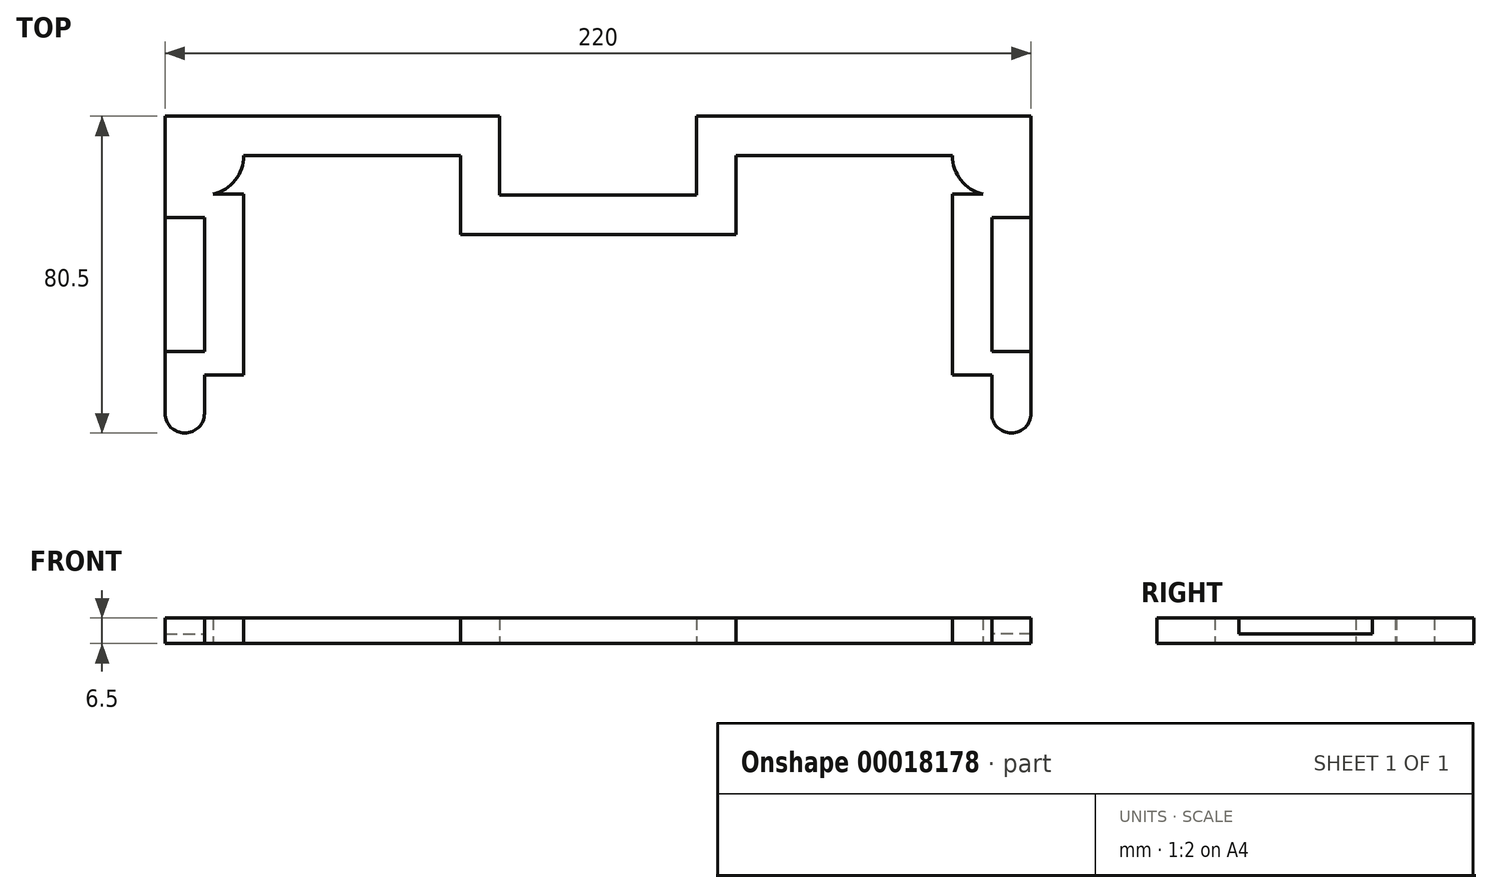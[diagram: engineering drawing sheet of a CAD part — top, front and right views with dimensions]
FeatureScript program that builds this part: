
annotation { "Feature Type Name" : "Feature", "Feature Type Description" : "" }
export const myFeature = defineFeature(function(context is Context, id is Id, definition is map)
    precondition{}
    {
        {
            var Q0;
            Q0=qCreatedBy(makeId("Top.planeOp"),FACE);
            var sketch = newSketch(context, id + "F0", { "sketchPlane" : qUnion([Q0])});
            skLineSegment(sketch, "E0.rect.top", {"start": v(110, 112.75) * mm, "end": v(25, 112.75) * mm});
            skLineSegment(sketch, "E0.rect.left", {"start": v(110, -112.75) * mm, "end": v(110, -112.72) * mm});
            skPoint(sketch, "E0.rect.middle", {"position": v(0, 0) * mm});
            skLineSegment(sketch, "E1.rect.top", {"start": v(-90, 102.75) * mm, "end": v(-35, 102.75) * mm});
            skLineSegment(sketch, "E1.rect.right", {"start": v(100, -102.75) * mm, "end": v(100, -102.7) * mm});
            skArc(sketch, "E2", {"start": v(90, 102.75) * mm, "mid": v(92.18, 96.51) * mm, "end": v(97.78, 93) * mm});
            skArc(sketch, "E3", {"start": v(-97.78, 93) * mm, "mid": v(-92.18, 96.51) * mm, "end": v(-90, 102.75) * mm});
            skLineSegment(sketch, "E4", {"start": v(0, -112.75) * mm, "end": v(0, 112.75) * mm, "construction": true});
            skLineSegment(sketch, "E5", {"start": v(-25, 112.75) * mm, "end": v(-25, 92.75) * mm});
            skLineSegment(sketch, "E6", {"start": v(-25, 92.75) * mm, "end": v(0, 92.75) * mm});
            skLineSegment(sketch, "E7", {"start": v(-35, 102.75) * mm, "end": v(-35, 82.75) * mm});
            skLineSegment(sketch, "E8", {"start": v(-35, 82.75) * mm, "end": v(0, 82.75) * mm});
            skLineSegment(sketch, "E9", {"start": v(-25, 92.75) * mm, "end": v(-25, 82.75) * mm, "construction": true});
            skLineSegment(sketch, "E10", {"start": v(-25, 92.75) * mm, "end": v(-35, 92.75) * mm, "construction": true});
            skLineSegment(sketch, "E11.MirrorCS", {"start": v(35, 82.75) * mm, "end": v(0, 82.75) * mm});
            skLineSegment(sketch, "E12.MirrorCS", {"start": v(25, 92.75) * mm, "end": v(0, 92.75) * mm});
            skLineSegment(sketch, "E13.MirrorCS", {"start": v(25, 112.75) * mm, "end": v(25, 92.75) * mm});
            skLineSegment(sketch, "E14.MirrorCS", {"start": v(35, 102.75) * mm, "end": v(35, 82.75) * mm});
            skLineSegment(sketch, "E15.trimOffspring", {"start": v(35, 102.75) * mm, "end": v(90, 102.75) * mm});
            skLineSegment(sketch, "E16.trimOffspring", {"start": v(-25, 112.75) * mm, "end": v(-110, 112.75) * mm});
            skLineSegment(sketch, "E17", {"start": v(126.96, -112.75) * mm, "end": v(126.96, 37.25) * mm, "construction": true});
            skLineSegment(sketch, "E18", {"start": v(126.96, 37.25) * mm, "end": v(110, 37.25) * mm, "construction": true});
            skLineSegment(sketch, "E19", {"start": v(110, 37.25) * mm, "end": v(100, 37.25) * mm, "construction": true});
            skArc(sketch, "E20", {"start": v(100, 37.25) * mm, "mid": v(105, 32.25) * mm, "end": v(110, 37.25) * mm});
            skArc(sketch, "E21.MirrorCS", {"start": v(-100, 37.25) * mm, "mid": v(-105, 32.25) * mm, "end": v(-110, 37.25) * mm});
            skLineSegment(sketch, "E22.trimOffspring", {"start": v(-100, 37.25) * mm, "end": v(-100, 47) * mm});
            skLineSegment(sketch, "E23.trimOffspring", {"start": v(-110, 37.25) * mm, "end": v(-110, 112.75) * mm});
            skLineSegment(sketch, "E24", {"start": v(100, 37.25) * mm, "end": v(100, 47) * mm});
            skLineSegment(sketch, "E25", {"start": v(100, -102.7) * mm, "end": v(100, 37.25) * mm, "construction": true});
            skLineSegment(sketch, "E26", {"start": v(110, -112.72) * mm, "end": v(110, 37.25) * mm, "construction": true});
            skLineSegment(sketch, "E27", {"start": v(110, 37.25) * mm, "end": v(110, 112.75) * mm});
            skLineSegment(sketch, "E28", {"start": v(100, 70) * mm, "end": v(-100, 70) * mm, "construction": true});
            skLineSegment(sketch, "E29", {"start": v(90, 93) * mm, "end": v(90, 70) * mm});
            skLineSegment(sketch, "E30.MirrorCS", {"start": v(100, 47) * mm, "end": v(90, 47) * mm});
            skLineSegment(sketch, "E31.MirrorCS", {"start": v(90, 47) * mm, "end": v(90, 70) * mm});
            skLineSegment(sketch, "E32.MirrorCS", {"start": v(-90, 47) * mm, "end": v(-90, 70) * mm});
            skLineSegment(sketch, "E33.MirrorCS", {"start": v(-90, 93) * mm, "end": v(-90, 70) * mm});
            skLineSegment(sketch, "E34.MirrorCS", {"start": v(-100, 47) * mm, "end": v(-90, 47) * mm});
            skLineSegment(sketch, "E35", {"start": v(90, 93) * mm, "end": v(97.78, 93) * mm});
            skLineSegment(sketch, "E36", {"start": v(-90, 93) * mm, "end": v(-97.78, 93) * mm});
            skSolve(sketch);
        }
        {
            var Q0;
            Q0 = qSketchRegion(id + "F0", true);
            extrude(context, id + "F1", {"entities" : qUnion([Q0]), "depth" : 6.5 * mm});
        }
        {
            var Q0;
            Q0=makeQuery(id+"F1.opExtrude","CAP_FACE",FACE,{"disambiguationData":[OSD([sQuery(id+"F0.wireOp",EDGE,"E0.rect.top"),sQuery(id+"F0.wireOp",EDGE,"E1.rect.top"),sQuery(id+"F0.wireOp",EDGE,"E2"),sQuery(id+"F0.wireOp",EDGE,"E3"),sQuery(id+"F0.wireOp",EDGE,"E5"),sQuery(id+"F0.wireOp",EDGE,"E6"),sQuery(id+"F0.wireOp",EDGE,"E7"),sQuery(id+"F0.wireOp",EDGE,"E8"),sQuery(id+"F0.wireOp",EDGE,"E11.MirrorCS"),sQuery(id+"F0.wireOp",EDGE,"E12.MirrorCS"),sQuery(id+"F0.wireOp",EDGE,"E13.MirrorCS"),sQuery(id+"F0.wireOp",EDGE,"E14.MirrorCS"),sQuery(id+"F0.wireOp",EDGE,"E15.trimOffspring"),sQuery(id+"F0.wireOp",EDGE,"E16.trimOffspring"),sQuery(id+"F0.wireOp",EDGE,"E20"),sQuery(id+"F0.wireOp",EDGE,"E21.MirrorCS"),sQuery(id+"F0.wireOp",EDGE,"E22.trimOffspring"),sQuery(id+"F0.wireOp",EDGE,"E23.trimOffspring"),sQuery(id+"F0.wireOp",EDGE,"E24"),sQuery(id+"F0.wireOp",EDGE,"E27"),sQuery(id+"F0.wireOp",EDGE,"E29"),sQuery(id+"F0.wireOp",EDGE,"E30.MirrorCS"),sQuery(id+"F0.wireOp",EDGE,"E31.MirrorCS"),sQuery(id+"F0.wireOp",EDGE,"E32.MirrorCS"),sQuery(id+"F0.wireOp",EDGE,"E33.MirrorCS"),sQuery(id+"F0.wireOp",EDGE,"E34.MirrorCS"),sQuery(id+"F0.wireOp",EDGE,"E35"),sQuery(id+"F0.wireOp",EDGE,"E36")])],"isStart":false});
            var sketch = newSketch(context, id + "F2", { "sketchPlane" : qUnion([Q0])});
            skLineSegment(sketch, "E37", {"start": v(0, 0) * mm, "end": v(0, 148.58) * mm, "construction": true});
            skLineSegment(sketch, "E38", {"start": v(110, 87) * mm, "end": v(100, 87) * mm});
            skLineSegment(sketch, "E39", {"start": v(100, 87) * mm, "end": v(100, 53) * mm});
            skLineSegment(sketch, "E40", {"start": v(100, 53) * mm, "end": v(110, 53) * mm});
            skPoint(sketch, "E41.startSnap0", {"position": v(100, 70) * mm});
            skLineSegment(sketch, "E42", {"start": v(90, 70) * mm, "end": v(100, 70) * mm, "construction": true});
            skLineSegment(sketch, "E43", {"start": v(110, 87) * mm, "end": v(110, 53) * mm});
            skLineSegment(sketch, "E44.MirrorCS", {"start": v(-110, 87) * mm, "end": v(-100, 87) * mm});
            skLineSegment(sketch, "E45.MirrorCS", {"start": v(-100, 87) * mm, "end": v(-100, 53) * mm});
            skLineSegment(sketch, "E46.MirrorCS", {"start": v(-100, 53) * mm, "end": v(-110, 53) * mm});
            skLineSegment(sketch, "E47.MirrorCS", {"start": v(-110, 87) * mm, "end": v(-110, 53) * mm});
            skSolve(sketch);
        }
        {
            var Q0;
            Q0 = qSketchRegion(id + "F2", true);
            extrude(context, id + "F3", {"entities" : qUnion([Q0]), "operationType" : NewBodyOperationType.REMOVE, "oppositeDirection" : true, "depth" : 4 * mm});
        }
    });
